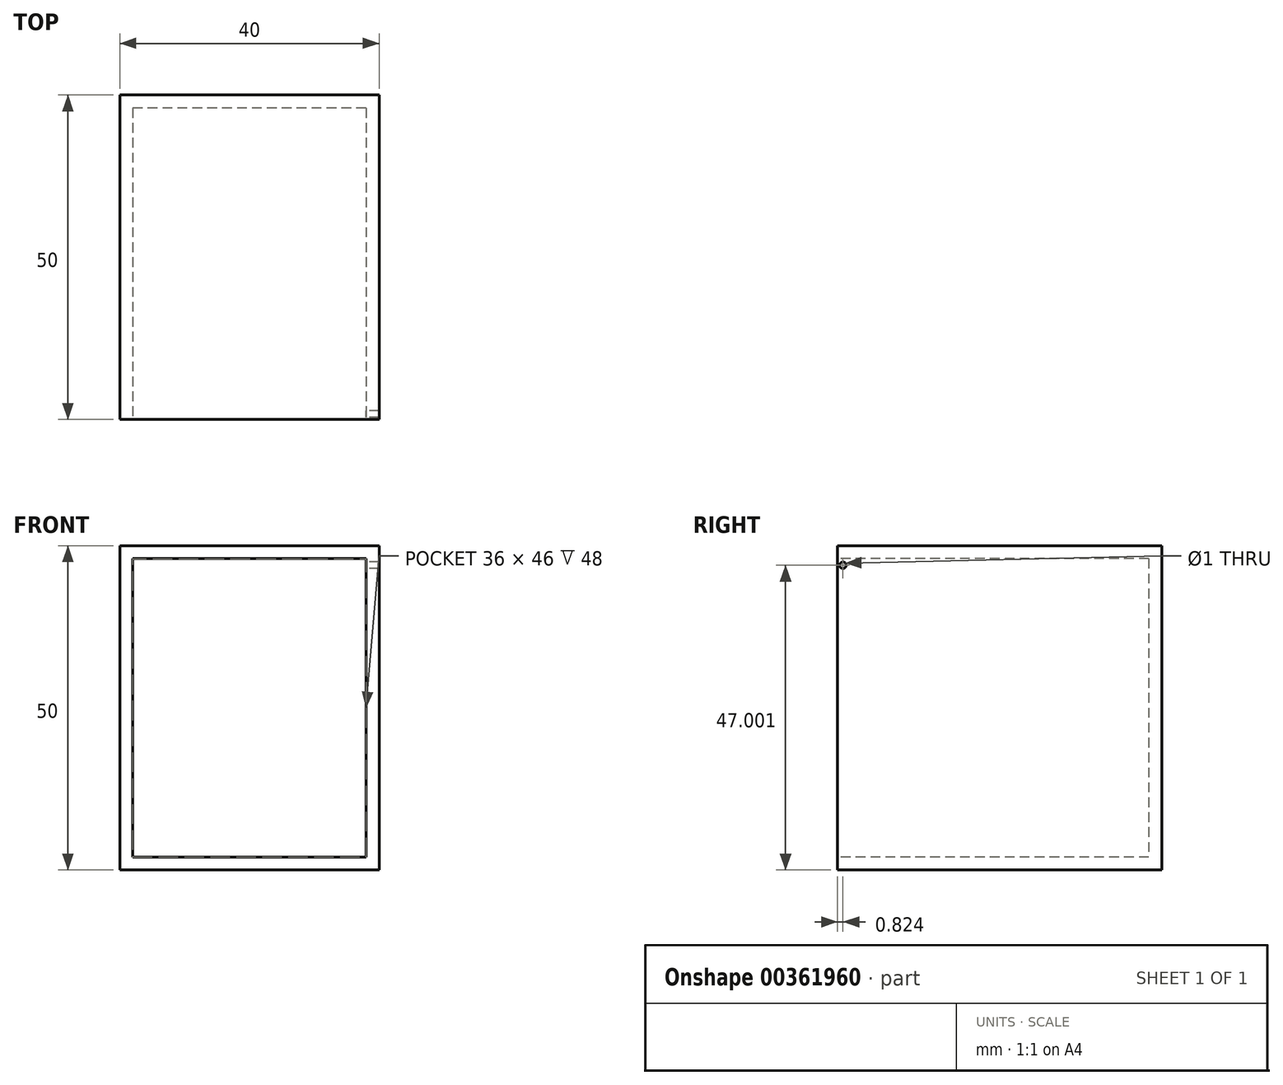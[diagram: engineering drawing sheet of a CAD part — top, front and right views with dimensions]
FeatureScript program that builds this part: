
annotation { "Feature Type Name" : "Feature", "Feature Type Description" : "" }
export const myFeature = defineFeature(function(context is Context, id is Id, definition is map)
    precondition{}
    {
        {
            var Q0;
            Q0=qCreatedBy(makeId("Top.planeOp"),FACE);
            var sketch = newSketch(context, id + "F0", { "sketchPlane" : qUnion([Q0])});
            skLineSegment(sketch, "E0.bottom", {"start": v(20, 25) * mm, "end": v(-20, 25) * mm});
            skLineSegment(sketch, "E0.top", {"start": v(20, -25) * mm, "end": v(-20, -25) * mm});
            skLineSegment(sketch, "E0.left", {"start": v(20, 25) * mm, "end": v(20, -25) * mm});
            skLineSegment(sketch, "E0.right", {"start": v(-20, 25) * mm, "end": v(-20, -25) * mm});
            skPoint(sketch, "E0.middle", {"position": v(0, 0) * mm});
            skSolve(sketch);
        }
        {
            var Q0;
            Q0=makeQuery(id+"F0.imprint","IMPRINT",FACE,{"disambiguationData":[TD([[makeQuery(id+"F0.imprint","IMPRINT",EDGE,{"derivedFrom":sQuery(id+"F0.wireOp",EDGE,"E0.bottom")}),1.0]])]});
            extrude(context, id + "F1", {"entities" : qUnion([Q0]), "depth" : 50 * mm});
        }
        {
            var Q0;
            Q0=makeQuery(id+"F1.opExtrude","SWEPT_FACE",FACE,{"disambiguationData":[OSD([sQuery(id+"F0.wireOp",EDGE,"E0.top")])]});
            shell(context, id + "F2", {"entities" : qUnion([Q0]), "thickness" : 2 * mm});
        }
        {
            var Q0;
            Q0=makeQuery(id+"F2.opShell","OFFSET_FACE",FACE,{"disambiguationData":[OSD([sQuery(id+"F0.wireOp",EDGE,"E0.left")])]});
            var sketch = newSketch(context, id + "F3", { "sketchPlane" : qUnion([Q0])});
            skCircle(sketch, "E1", {"center": v(24.18, 47) * mm, "radius": 0.5 * mm});
            skSolve(sketch);
        }
        {
            var Q0;
            Q0 = qSketchRegion(id + "F3", true);
            extrude(context, id + "F4", {"entities" : qUnion([Q0]), "operationType" : NewBodyOperationType.REMOVE, "oppositeDirection" : true, "depth" : 25 * mm});
        }
    });
